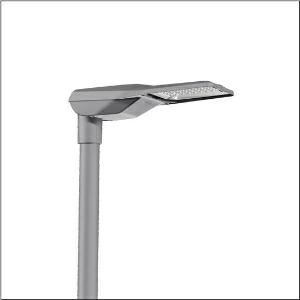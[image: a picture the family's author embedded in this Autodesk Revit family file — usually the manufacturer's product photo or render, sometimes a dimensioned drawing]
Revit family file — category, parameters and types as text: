
# Revit family: streetlight_sl_21_mini___st1_0a_5xe6d43a08jb_fa98
name_source: partatom
category: Lighting Fixtures
units: mm (PartAtom-declared; Revit-internal decimal feet)

## family parameters
Cut with Voids When Loaded = No
Host = Face
Light Source = No
Part Type = Normal
Room Calculation Point = No
Round Connector Dimension = Use Diameter
Shared = No

## types (1)
- --- (1 x LED, 13390 lm, 87.3 W, 4000K)
    Apparent Load = 87 VA
    CIE Flux Codes = 40 73 97 100 100
    Color Rendering = 70
    Color Temperature = 4000K
    Default Elevation = 1800 mm
    Description = Streetlight SL 21 mini, mast luminaire, primary light control with lens, of PMMA, primary optical cover: cover, of toughened safety glass, transparent, light distribution: ST1.0a, light emission: direct distribution, primary light characteristic: asymmetric, installation type: post-top, side-entry, LED, 3G 1.5mm², High Power LED, rated luminous flux: 13.390lm, luminous efficacy: 153lm/W, light colour: 740, colour temperature: 4000K, control: overheat protection, constant luminous flux control, time-dependent luminous flux control, flexible luminous flux parameterisation, mains connection: 230..240V, AC, 50/60Hz, connection cable pre-assembled, cable length: 10,5m, wiring characteristics: H07RN-F, start of lifetime: 87W, end of service life: 90W, reduction: 40W, luminaire housing, of diecast aluminium, powder-coated, Siteco® metallic grey (DB 702S), corrosivity category C5 mid according to DIN EN ISO 12944, please order mast flange separately, inclination adjustable: 0°, 5°, 10°, 15°, sealing non-destructively replaceable, multi-level sealing system, length: 628mm, width: 235mm, height: 110mm, mast flange for spigot size: 42mm (side-entry): 5XC10008XM4, 60/48mm (side-entry/post-top): 5XC10108XM2, 76/60mm (side-entry/post-top): 5XC10108XM1, protection rating (complete): IP66, insulation class (complete): insulation class II (safety insulation), certification: CE, ENEC, ENEC+, VDE, impact resistance: IK09, permissible operating ambient temperature for outdoor applications: -40..+50°C, standard-compliant lighting for roads and squares, packaging unit: 1 piece

Light Distribution: ST1.0a
    Height = 110 mm
    Lamp = 1 x LED
    Lamp Light Flux = 13390 lm
    Lamp Power = 87.3 W
    Lamp count = 1
    Length = 625 mm
    Luminous efficacy = 153 lm/W
    Manufacturer = Siteco
    ModVariant = No
    Model = 5XE6D43A08JB
    Number of Poles = 1
    OnlyDefault = Yes
    Power Factor = 1
    Product Name = Streetlight SL 21 mini | ST1.0a
    Product group = mast luminaire | pylon top
    ProductGroupID = 6100
    Protection Class = Protection class II
    Protection Degree = IP 66
    RLX_Detail_Level = 1
    RLX_Emergency_Light_Flux = 0 lm
    RLX_Emergency_Type = 0
    RLX_Emergency_Type_DB = No
    RlxData = <blob elided: 92297 chars, md5=8a3e908f>
    Socket = socket
    Standby Power = 0 W
    System Light Flux = 13390 lm
    System Power = 87 W
    Type Comments = factory setting: luminous flux: 100 % | Output Level: 100 % | 915 mA
    Type Image = l_1003519.jpg
    URL = http://relux.com
    VarID = @adj_103743
    Voltage = 0 V
    Weight = 0.00 kg
    Width = 234 mm

## geometry (parser evidence)
native form markers: Blend x4, Sweep x11
no freeform markers — native parametric forms only
